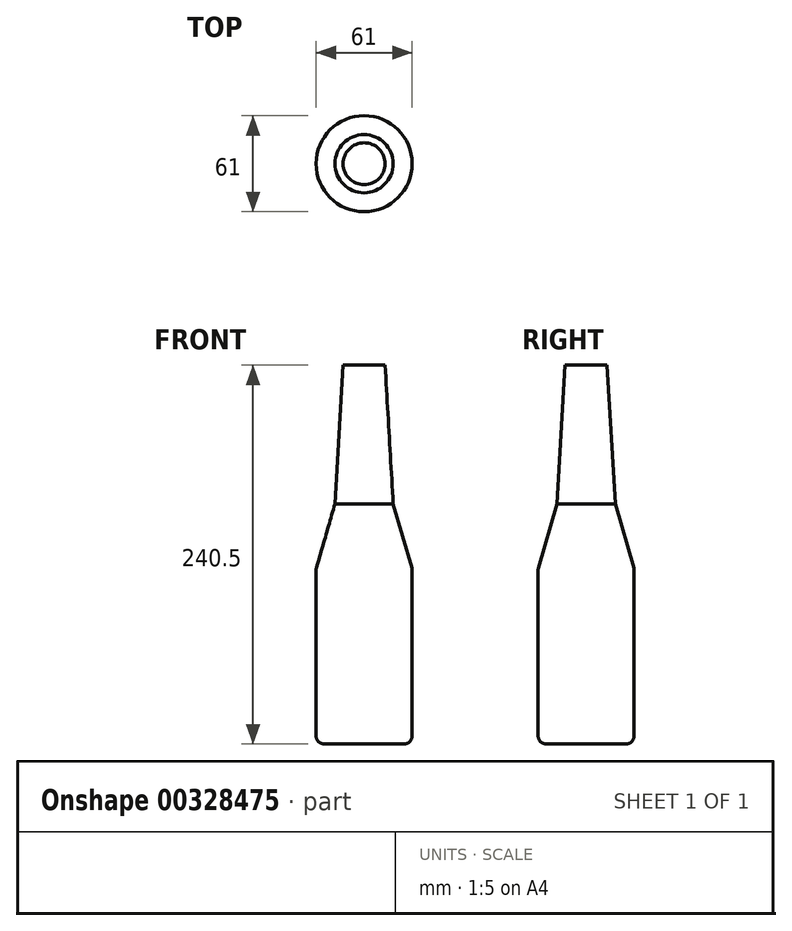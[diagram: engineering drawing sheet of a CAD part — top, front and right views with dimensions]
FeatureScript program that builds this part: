
annotation { "Feature Type Name" : "Feature", "Feature Type Description" : "" }
export const myFeature = defineFeature(function(context is Context, id is Id, definition is map)
    precondition{}
    {
        {
            var Q0;
            Q0=qCreatedBy(makeId("Top.planeOp"),FACE);
            var sketch = newSketch(context, id + "F0", { "sketchPlane" : qUnion([Q0])});
            skCircle(sketch, "E0", {"center": v(0, 0) * mm, "radius": 30.5 * mm});
            skSolve(sketch);
        }
        {
            var Q0;
            Q0=qCreatedBy(makeId("Top.planeOp"),FACE);
            cPlane(context, id + "F1", {"entities" : qUnion([Q0]), "cplaneType" : CPlaneType.OFFSET, "offset" : 152.5 * mm, "width" : 150 * mm, "height" : 150 * mm});
        }
        {
            var Q0;
            Q0=makeQuery(id+"F0.imprint","IMPRINT",FACE,{"disambiguationData":[TD([[makeQuery(id+"F0.imprint","IMPRINT",EDGE,{"derivedFrom":sQuery(id+"F0.wireOp",EDGE,"E0")}),1.0]])]});
            extrude(context, id + "F2", {"entities" : qUnion([Q0]), "depth" : 111 * mm});
        }
        {
            var Q0;
            Q0=qCreatedBy(id+"F1.planeOp",FACE);
            var sketch = newSketch(context, id + "F3", { "sketchPlane" : qUnion([Q0])});
            skCircle(sketch, "E1", {"center": v(0, 0) * mm, "radius": 18.5 * mm});
            skSolve(sketch);
        }
        {
            var Q1;
            Q1=makeQuery(id+"F2.opExtrude","CAP_FACE",FACE,{"disambiguationData":[OSD([sQuery(id+"F0.wireOp",EDGE,"E0")])],"isStart":false});
            var Q2;
            Q2=makeQuery(id+"F3.imprint","IMPRINT",FACE,{"disambiguationData":[TD([[makeQuery(id+"F3.imprint","IMPRINT",EDGE,{"derivedFrom":sQuery(id+"F3.wireOp",EDGE,"E1")}),1.0]])]});
            loft(context, id + "F4", {"operationType" : NewBodyOperationType.ADD, "sheetProfilesArray" : [{ "sheetProfileEntities" : qUnion([Q1]) }, { "sheetProfileEntities" : qUnion([Q2]) }]});
        }
        {
            var Q0;
            {var subQ0=sQuery(id+"F0.wireOp",EDGE,"E0");Q0=makeQuery(id+"F4.boolean.opBoolean","MERGE",EDGE,{"derivedFrom":[makeQuery(id+"F2.opExtrude","CAP_EDGE",EDGE,{"disambiguationData":[OSD([subQ0])],"isStart":false}),makeQuery(id+"F4.opLoft","MID_CAP_EDGE",EDGE,{"disambiguationData":[OSD([subQ0])],"capPos":0.0})]});}
            fillet(context, id + "F5", {"entities" : qUnion([Q0]), "radius" : 5 * mm, "tangentPropagation" : true, "allowEdgeOverflow" : false});
        }
        {
            var Q0;
            Q0=makeQuery(id+"F2.opExtrude","CAP_EDGE",EDGE,{"disambiguationData":[OSD([sQuery(id+"F0.wireOp",EDGE,"E0")])],"isStart":true});
            fillet(context, id + "F6", {"entities" : qUnion([Q0]), "radius" : 5 * mm, "tangentPropagation" : true, "allowEdgeOverflow" : false});
        }
        {
            var Q0;
            Q0=qCreatedBy(id+"F1.planeOp",FACE);
            cPlane(context, id + "F7", {"entities" : qUnion([Q0]), "cplaneType" : CPlaneType.OFFSET, "offset" : 88 * mm, "width" : 150 * mm, "height" : 150 * mm});
        }
        {
            var Q0;
            Q0=qCreatedBy(id+"F7.planeOp",FACE);
            var sketch = newSketch(context, id + "F8", { "sketchPlane" : qUnion([Q0])});
            skCircle(sketch, "E2", {"center": v(0, 0) * mm, "radius": 13.3 * mm});
            skSolve(sketch);
        }
        {
            var Q1;
            Q1=makeQuery(id+"F4.opLoft","CAP_FACE",FACE,{"disambiguationData":[OSD([makeQuery(id+"F3.imprint","IMPRINT",FACE,{"disambiguationData":[TD([[makeQuery(id+"F3.imprint","IMPRINT",EDGE,{"derivedFrom":sQuery(id+"F3.wireOp",EDGE,"E1")}),1.0]])]})])],"isStart":true});
            var Q2;
            Q2=makeQuery(id+"F8.imprint","IMPRINT",FACE,{"disambiguationData":[TD([[makeQuery(id+"F8.imprint","IMPRINT",EDGE,{"derivedFrom":sQuery(id+"F8.wireOp",EDGE,"E2")}),1.0]])]});
            loft(context, id + "F9", {"operationType" : NewBodyOperationType.ADD, "sheetProfilesArray" : [{ "sheetProfileEntities" : qUnion([Q1]) }, { "sheetProfileEntities" : qUnion([Q2]) }]});
        }
    });
